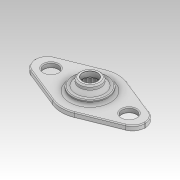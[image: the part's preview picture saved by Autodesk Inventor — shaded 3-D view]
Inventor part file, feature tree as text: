
AUTODESK INVENTOR PART (.ipt)
format: ipt  version: 2020 (Build 240168000, 168)  size: 983,040 bytes
history: native  units: mm
features: sketch x8, other x7, extrude x6, revolve x3, fillet x3, pattern_circular x1, imported_body x1
ambient origin geometry x8: Origin, YZ Plane, XZ Plane, XY Plane, X Axis, Y Axis, Z Axis, Center Point
bodies: Solid1 (feature_tree)
feature tree (29):
  other  "HD_mastersketch.ipt"
  other  "Blocks"
  revolve  "Revolution1"  [1 undecoded]
  extrude  "Extrusion1"  Depth=5.0mm
  extrude  "Extrusion2"  TaperAngle=0.0deg  [1 undecoded]
  fillet  "Fillet1"  [1 undecoded]
  extrude  "Extrusion7"  Depth=7.0mm
  extrude  "Extrusion10"  TaperAngle=0.0deg  [1 undecoded]
  pattern_circular  "Circular Pattern1"  Angle=90.0deg  [1 undecoded]
  revolve  "Revolution3"  [1 undecoded]
  fillet  "Fillet5"  Radius=0.8mm
  fillet  "Fillet6"  Radius=10.9mm
  revolve  "Revolution4"  [1 undecoded]
  extrude  "Extrusion8"  Depth=200.0mm TaperAngle=360.0deg
  extrude  "Extrusion9"  Depth=0.2mm
  other  "608 bearing"
  other  "Belt"
  other  "Rotor"
  imported_body  "Base"
  sketch  "Sketch8"  dims[d1=10.0mm d24=7.0mm d25=22.0mm d26=8.0mm]
  sketch  "Sketch9"  dims[d2=90.0deg d3=5.0mm d4=10.0mm]
  sketch  "Sketch15"  dims[d5=15.0mm d6=0.0mm d7=0.0mm d8=0.0mm d9=0.0mm]
  sketch  "Sketch16"  dims[d10=7.0mm d44=12.6mm]
  sketch  "Sketch17"  dims[d45=10.0mm d46=0.0mm d47=0.0mm d48=0.0mm]
  sketch  "Sketch18"  dims[d49=4.5mm d50=0.0mm]
  sketch  "Sketch19"  dims[d51=8.726646mm]
  sketch  "Sketch20"  dims[d52=1.0mm d53=90.0deg d54=0.5mm d55=0.8mm d56=10.9mm d58=4.5mm d59=0.0mm d60=200.0mm d61=360.0deg d63=0.2mm d68=6.0mm d69=4.1mm d70=4.2mm d72=45.0deg d73=2.0mm d74=0.75mm d75=0.75mm d76=0.1mm d77=0.1mm d78=90.0deg d79=0.8mm d80=45.0deg d81=45.0deg d82=12.6mm]
  other  "608 bearing:1"
  other  "608 bearing:2"
note: 7 required parameter values undecoded (feature->parameter linkage not recoverable at this tier; creation-order binding heuristic only, values carry confidence <= 0.55)